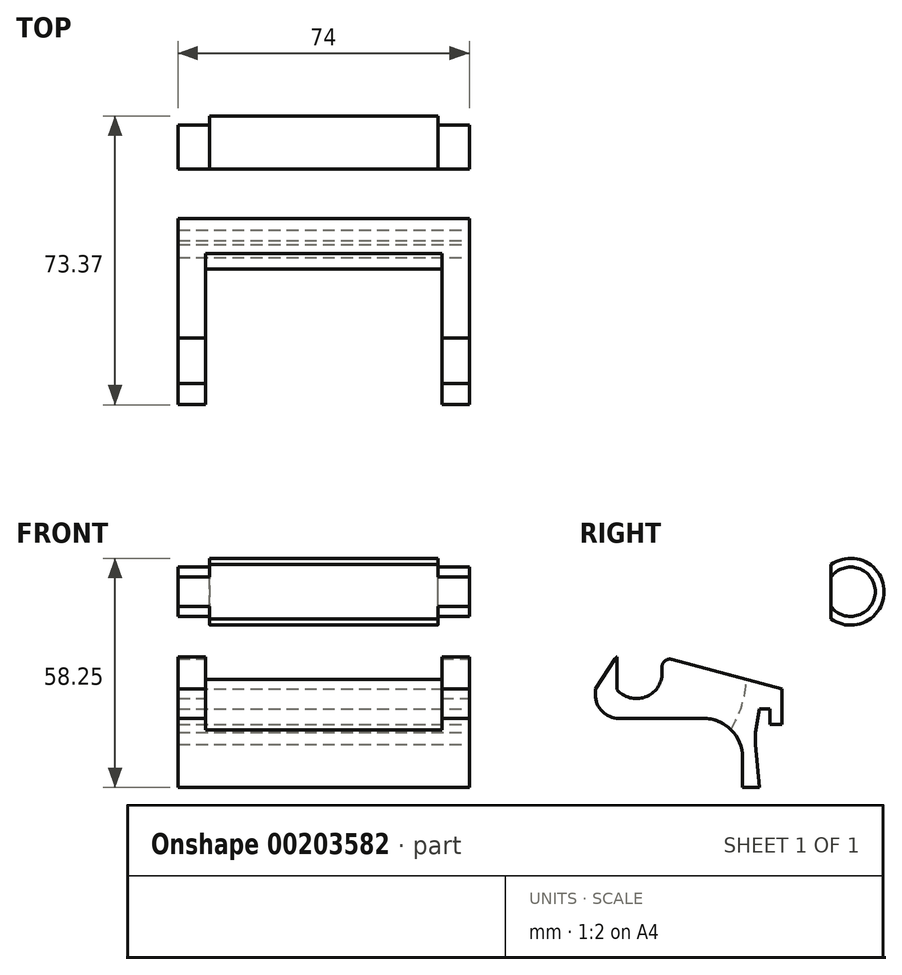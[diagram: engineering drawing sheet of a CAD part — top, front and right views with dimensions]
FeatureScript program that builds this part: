
annotation { "Feature Type Name" : "Feature", "Feature Type Description" : "" }
export const myFeature = defineFeature(function(context is Context, id is Id, definition is map)
    precondition{}
    {
        {
            var Q0;
            Q0=qCreatedBy(makeId("Right.planeOp"),FACE);
            var sketch = newSketch(context, id + "F0", { "sketchPlane" : qUnion([Q0])});
            skLineSegment(sketch, "E0", {"start": v(-64.23, -24.7) * mm, "end": v(-64.23, -4.7) * mm});
            skLineSegment(sketch, "E1", {"start": v(-64.23, -4.7) * mm, "end": v(-61.53, -4.7) * mm});
            skLineSegment(sketch, "E2", {"start": v(-61.53, -4.7) * mm, "end": v(-61.53, -8.7) * mm});
            skLineSegment(sketch, "E3", {"start": v(-61.53, -8.7) * mm, "end": v(-58.53, -8.7) * mm});
            skLineSegment(sketch, "E4", {"start": v(-58.53, -8.7) * mm, "end": v(-58.53, 0.3) * mm});
            skLineSegment(sketch, "E5", {"start": v(-58.53, 0.3) * mm, "end": v(-67.9, 0.3) * mm});
            skLineSegment(sketch, "E6", {"start": v(-67.9, 0.3) * mm, "end": v(-105.89, 0.3) * mm});
            skLineSegment(sketch, "E7", {"start": v(-105.89, 0.3) * mm, "end": v(-105.89, -1.11) * mm});
            skLineSegment(sketch, "E8", {"start": v(-99.89, -7.11) * mm, "end": v(-78.49, -7.11) * mm});
            skLineSegment(sketch, "E9", {"start": v(-68.49, -17.11) * mm, "end": v(-68.49, -24.7) * mm});
            skLineSegment(sketch, "E10", {"start": v(-68.49, -24.7) * mm, "end": v(-64.23, -24.7) * mm});
            skCircle(sketch, "E11", {"center": v(-95.44, 4.39) * mm, "radius": 28 * mm});
            skCircle(sketch, "E12", {"center": v(-95.44, 4.39) * mm, "radius": 6.5 * mm});
            skLineSegment(sketch, "E13", {"start": v(-100.44, 8.54) * mm, "end": v(-100.44, 0.23) * mm});
            skLineSegment(sketch, "E14", {"start": v(-105.89, 0.3) * mm, "end": v(-100.88, 7.95) * mm});
            skLineSegment(sketch, "E15", {"start": v(-88.94, 0.3) * mm, "end": v(-88.94, 5.93) * mm});
            skLineSegment(sketch, "E16", {"start": v(-86.42, 7.86) * mm, "end": v(-58.53, 0.3) * mm});
            skPoint(sketch, "E17.visualSharp", {"position": v(-105.89, -7.11) * mm});
            skArc(sketch, "E17.filletArc", {"start": v(-105.89, -1.11) * mm, "mid": v(-104.13, -5.36) * mm, "end": v(-99.89, -7.11) * mm});
            skPoint(sketch, "E18.visualSharp", {"position": v(-68.49, -7.11) * mm});
            skArc(sketch, "E18.filletArc", {"start": v(-68.49, -17.11) * mm, "mid": v(-71.42, -10.04) * mm, "end": v(-78.49, -7.11) * mm});
            skPoint(sketch, "E19.visualSharp", {"position": v(-88.94, 8.54) * mm});
            skArc(sketch, "E19.filletArc", {"start": v(-86.42, 7.86) * mm, "mid": v(-88.15, 7.52) * mm, "end": v(-88.94, 5.93) * mm});
            skLineSegment(sketch, "E20", {"start": v(-64.23, -10.7) * mm, "end": v(-65.23, -10.7) * mm});
            skLineSegment(sketch, "E21", {"start": v(-65.23, -10.7) * mm, "end": v(-65.23, -13.7) * mm});
            skLineSegment(sketch, "E22", {"start": v(-65.23, -13.7) * mm, "end": v(-64.23, -13.7) * mm});
            skLineSegment(sketch, "E23", {"start": v(-64.23, -4.7) * mm, "end": v(-65.23, -10.7) * mm});
            skLineSegment(sketch, "E24", {"start": v(-65.23, -13.7) * mm, "end": v(-64.23, -24.7) * mm});
            skSolve(sketch);
        }
        {
            var Q0;
            {var subQ8=sQuery(id+"F0.wireOp",EDGE,"E7");Q0=makeQuery(id+"F0.imprint","IMPRINT",FACE,{"disambiguationData":[TD([[makeQuery(id+"F0.imprint","IMPRINT",EDGE,{"derivedFrom":subQ8}),1.0]])]});}
            var Q1;
            {var subQ0=sQuery(id+"F0.wireOp",EDGE,"E13");var subQ1=sQuery(id+"F0.wireOp",EDGE,"E6");var subQ2=makeQuery(id+"F0.imprint","INTERSECT",VERTEX,{"derivedFrom":[subQ1,subQ0]});Q1=makeQuery(id+"F0.imprint","IMPRINT",FACE,{"disambiguationData":[TD([[makeQuery(id+"F0.imprint","IMPRINT",EDGE,{"disambiguationData":[TD([[subQ2,-1.0]])],"derivedFrom":subQ1}),1.0]])]});}
            var Q2;
            {var subQ0=sQuery(id+"F0.wireOp",EDGE,"E13");var subQ1=sQuery(id+"F0.wireOp",EDGE,"E6");var subQ2=makeQuery(id+"F0.imprint","INTERSECT",VERTEX,{"derivedFrom":[subQ1,subQ0]});Q2=makeQuery(id+"F0.imprint","IMPRINT",FACE,{"disambiguationData":[TD([[makeQuery(id+"F0.imprint","IMPRINT",EDGE,{"disambiguationData":[TD([[subQ2,-1.0]])],"derivedFrom":subQ1}),-1.0]])]});}
            var Q3;
            {var subQ0=sQuery(id+"F0.wireOp",EDGE,"E14");Q3=makeQuery(id+"F0.imprint","IMPRINT",FACE,{"disambiguationData":[TD([[makeQuery(id+"F0.imprint","IMPRINT",EDGE,{"derivedFrom":subQ0}),-1.0]])]});}
            var Q4;
            {var subQ0=sQuery(id+"F0.wireOp",EDGE,"E15");Q4=makeQuery(id+"F0.imprint","IMPRINT",FACE,{"disambiguationData":[TD([[makeQuery(id+"F0.imprint","IMPRINT",EDGE,{"derivedFrom":subQ0}),-1.0]])]});}
            var Q5;
            {var subQ5=sQuery(id+"F0.wireOp",EDGE,"E1");Q5=makeQuery(id+"F0.imprint","IMPRINT",FACE,{"disambiguationData":[TD([[makeQuery(id+"F0.imprint","IMPRINT",EDGE,{"derivedFrom":subQ5}),1.0]])]});}
            var Q6;
            {var subQ0=sQuery(id+"F0.wireOp",EDGE,"E16");var subQ3=sQuery(id+"F0.wireOp",EDGE,"E11");var subQ5=makeQuery(id+"F0.imprint","INTERSECT",VERTEX,{"derivedFrom":[subQ3,subQ0]});Q6=makeQuery(id+"F0.imprint","IMPRINT",FACE,{"disambiguationData":[TD([[makeQuery(id+"F0.imprint","IMPRINT",EDGE,{"disambiguationData":[TD([[subQ5,1.0]])],"derivedFrom":subQ3}),-1.0]])]});}
            var Q7;
            {var subQ0=sQuery(id+"F0.wireOp",EDGE,"E15");var subQ1=sQuery(id+"F0.wireOp",EDGE,"E6");var subQ2=makeQuery(id+"F0.imprint","INTERSECT",VERTEX,{"derivedFrom":[subQ1,subQ0]});Q7=makeQuery(id+"F0.imprint","IMPRINT",FACE,{"disambiguationData":[TD([[makeQuery(id+"F0.imprint","IMPRINT",EDGE,{"disambiguationData":[TD([[subQ2,-1.0]])],"derivedFrom":subQ1}),-1.0]])]});}
            extrude(context, id + "F1", {"entities" : qUnion([Q0, Q1, Q2, Q3, Q4, Q5, Q6, Q7]), "oppositeDirection" : true, "depth" : 37 * mm, "hasSecondDirection" : true, "secondDirectionOppositeDirection" : false, "secondDirectionDepth" : 37 * mm});
        }
        {
            var Q0;
            Q0=makeQuery(id+"F0.imprint","IMPRINT",FACE,{"disambiguationData":[TD([[makeQuery(id+"F0.imprint","IMPRINT",EDGE,{"derivedFrom":sQuery(id+"F0.wireOp",EDGE,"E7")}),-1.0]])]});
            var Q1;
            {var subQ0=sQuery(id+"F0.wireOp",EDGE,"E12");var subQ1=sQuery(id+"F0.wireOp",EDGE,"E6");var subQ2=makeQuery(id+"F0.imprint","INTERSECT",VERTEX,{"disambiguationData":[OD(0.0)],"derivedFrom":[subQ1,subQ0]});Q1=makeQuery(id+"F0.imprint","IMPRINT",FACE,{"disambiguationData":[TD([[makeQuery(id+"F0.imprint","IMPRINT",EDGE,{"disambiguationData":[TD([[subQ2,-1.0]])],"derivedFrom":subQ1}),-1.0]])]});}
            var Q2;
            {var subQ0=sQuery(id+"F0.wireOp",EDGE,"E12");var subQ1=sQuery(id+"F0.wireOp",EDGE,"E6");var subQ2=makeQuery(id+"F0.imprint","INTERSECT",VERTEX,{"disambiguationData":[OD(0.0)],"derivedFrom":[subQ1,subQ0]});Q2=makeQuery(id+"F0.imprint","IMPRINT",FACE,{"disambiguationData":[TD([[makeQuery(id+"F0.imprint","IMPRINT",EDGE,{"disambiguationData":[TD([[subQ2,-1.0]])],"derivedFrom":subQ1}),1.0]])]});}
            var Q3;
            {var subQ0=sQuery(id+"F0.wireOp",EDGE,"E13");var subQ1=sQuery(id+"F0.wireOp",EDGE,"E6");var subQ2=makeQuery(id+"F0.imprint","INTERSECT",VERTEX,{"derivedFrom":[subQ1,subQ0]});Q3=makeQuery(id+"F0.imprint","IMPRINT",FACE,{"disambiguationData":[TD([[makeQuery(id+"F0.imprint","IMPRINT",EDGE,{"disambiguationData":[TD([[subQ2,-1.0]])],"derivedFrom":subQ1}),-1.0]])]});}
            var Q4;
            {var subQ0=sQuery(id+"F0.wireOp",EDGE,"E13");var subQ1=sQuery(id+"F0.wireOp",EDGE,"E6");var subQ2=makeQuery(id+"F0.imprint","INTERSECT",VERTEX,{"derivedFrom":[subQ1,subQ0]});Q4=makeQuery(id+"F0.imprint","IMPRINT",FACE,{"disambiguationData":[TD([[makeQuery(id+"F0.imprint","IMPRINT",EDGE,{"disambiguationData":[TD([[subQ2,-1.0]])],"derivedFrom":subQ1}),1.0]])]});}
            var Q5;
            {var subQ8=sQuery(id+"F0.wireOp",EDGE,"E7");Q5=makeQuery(id+"F0.imprint","IMPRINT",FACE,{"disambiguationData":[TD([[makeQuery(id+"F0.imprint","IMPRINT",EDGE,{"derivedFrom":subQ8}),1.0]])]});}
            var Q6;
            {var subQ0=sQuery(id+"F0.wireOp",EDGE,"E15");Q6=makeQuery(id+"F0.imprint","IMPRINT",FACE,{"disambiguationData":[TD([[makeQuery(id+"F0.imprint","IMPRINT",EDGE,{"derivedFrom":subQ0}),-1.0]])]});}
            var Q7;
            {var subQ0=sQuery(id+"F0.wireOp",EDGE,"E14");Q7=makeQuery(id+"F0.imprint","IMPRINT",FACE,{"disambiguationData":[TD([[makeQuery(id+"F0.imprint","IMPRINT",EDGE,{"derivedFrom":subQ0}),-1.0]])]});}
            var Q8;
            {var subQ0=sQuery(id+"F0.wireOp",EDGE,"E15");var subQ1=sQuery(id+"F0.wireOp",EDGE,"E6");var subQ2=makeQuery(id+"F0.imprint","INTERSECT",VERTEX,{"derivedFrom":[subQ1,subQ0]});Q8=makeQuery(id+"F0.imprint","IMPRINT",FACE,{"disambiguationData":[TD([[makeQuery(id+"F0.imprint","IMPRINT",EDGE,{"disambiguationData":[TD([[subQ2,-1.0]])],"derivedFrom":subQ1}),-1.0]])]});}
            extrude(context, id + "F2", {"entities" : qUnion([Q0, Q1, Q2, Q3, Q4, Q5, Q6, Q7, Q8]), "operationType" : NewBodyOperationType.REMOVE, "oppositeDirection" : true, "depth" : 30 * mm, "hasSecondDirection" : true, "secondDirectionOppositeDirection" : false, "secondDirectionDepth" : 30 * mm});
        }
        {
            var Q0;
            Q0=qCreatedBy(makeId("Right.planeOp"),FACE);
            var sketch = newSketch(context, id + "F3", { "sketchPlane" : qUnion([Q0])});
            skCircle(sketch, "E25", {"center": v(-41.02, 25.05) * mm, "radius": 8.5 * mm});
            skSolve(sketch);
        }
        {
            var Q0;
            Q0=makeQuery(id+"F3.imprint","IMPRINT",FACE,{"disambiguationData":[TD([[makeQuery(id+"F3.imprint","IMPRINT",EDGE,{"derivedFrom":sQuery(id+"F3.wireOp",EDGE,"E25")}),1.0]])]});
            extrude(context, id + "F4", {"entities" : qUnion([Q0]), "depth" : 37 * mm, "hasSecondDirection" : true, "secondDirectionOppositeDirection" : true, "secondDirectionDepth" : 37 * mm});
        }
        {
            var Q0;
            Q0=makeQuery(id+"F4.opExtrude","CAP_FACE",FACE,{"disambiguationData":[OSD([sQuery(id+"F3.wireOp",EDGE,"E25")])],"isStart":false});
            var sketch = newSketch(context, id + "F5", { "sketchPlane" : qUnion([Q0])});
            skCircle(sketch, "E26.0", {"center": v(-41.02, 25.05) * mm, "radius": 8.5 * mm});
            skLineSegment(sketch, "E27", {"start": v(-46.02, 31.92) * mm, "end": v(-46.02, 18.17) * mm});
            skSolve(sketch);
        }
        {
            var Q0;
            {var subQ0=sQuery(id+"F5.wireOp",EDGE,"E27");Q0=makeQuery(id+"F5.imprint","IMPRINT",FACE,{"disambiguationData":[TD([[makeQuery(id+"F5.imprint","IMPRINT",EDGE,{"derivedFrom":subQ0}),-1.0]])]});}
            extrude(context, id + "F6", {"entities" : qUnion([Q0]), "operationType" : NewBodyOperationType.REMOVE, "endBound" : BoundingType.THROUGH_ALL, "oppositeDirection" : true, "depth" : 8 * mm});
        }
        {
            var Q0;
            Q0=makeQuery(id+"F4.opExtrude","CAP_FACE",FACE,{"disambiguationData":[OSD([sQuery(id+"F3.wireOp",EDGE,"E25")])],"isStart":false});
            var sketch = newSketch(context, id + "F7", { "sketchPlane" : qUnion([Q0])});
            skCircle(sketch, "E28", {"center": v(-41.02, 25.05) * mm, "radius": 6.25 * mm});
            skSolve(sketch);
        }
        {
            var Q0;
            {var subQ4=makeQuery(id+"F4.opExtrude","CAP_EDGE",EDGE,{"disambiguationData":[OSD([sQuery(id+"F3.wireOp",EDGE,"E25")])],"isStart":false});Q0=makeQuery(id+"F7.imprint","IMPRINT",FACE,{"disambiguationData":[TD([[makeQuery(id+"F7.imprint","IMPRINT",EDGE,{"derivedFrom":subQ4}),1.0]])]});}
            extrude(context, id + "F8", {"entities" : qUnion([Q0]), "operationType" : NewBodyOperationType.REMOVE, "oppositeDirection" : true, "depth" : 8 * mm});
        }
        {
            var Q0;
            Q0=makeQuery(id+"F4.opExtrude","CAP_FACE",FACE,{"disambiguationData":[OSD([sQuery(id+"F3.wireOp",EDGE,"E25")])],"isStart":true});
            var sketch = newSketch(context, id + "F9", { "sketchPlane" : qUnion([Q0])});
            skCircle(sketch, "E29", {"center": v(41.02, 25.05) * mm, "radius": 6.25 * mm});
            skSolve(sketch);
        }
        {
            var Q0;
            {var subQ1=sQuery(id+"F3.wireOp",EDGE,"E25");var subQ5=makeQuery(id+"F4.opExtrude","CAP_EDGE",EDGE,{"disambiguationData":[OSD([subQ1])],"isStart":true});Q0=makeQuery(id+"F9.imprint","IMPRINT",FACE,{"disambiguationData":[TD([[makeQuery(id+"F9.imprint","IMPRINT",EDGE,{"derivedFrom":subQ5}),-1.0]])]});}
            extrude(context, id + "F10", {"entities" : qUnion([Q0]), "operationType" : NewBodyOperationType.REMOVE, "oppositeDirection" : true, "depth" : 8 * mm});
        }
    });
